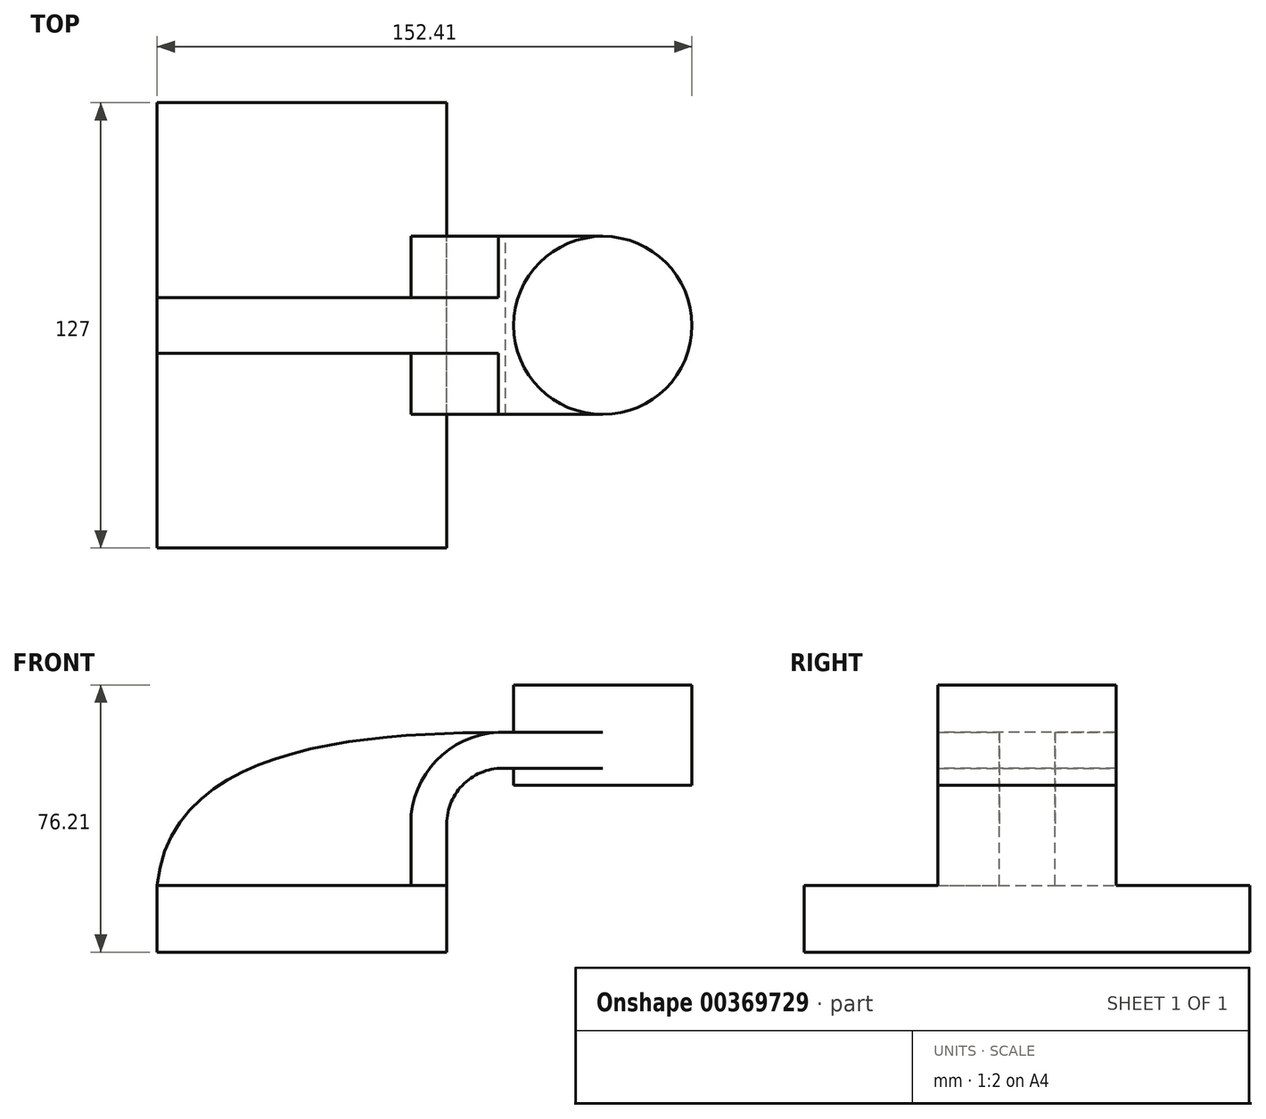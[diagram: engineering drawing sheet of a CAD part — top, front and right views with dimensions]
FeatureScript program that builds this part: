
annotation { "Feature Type Name" : "Feature", "Feature Type Description" : "" }
export const myFeature = defineFeature(function(context is Context, id is Id, definition is map)
    precondition{}
    {
        {
            var Q0;
            Q0=qCreatedBy(makeId("Front.planeOp"),FACE);
            var sketch = newSketch(context, id + "F0", { "sketchPlane" : qUnion([Q0])});
            skLineSegment(sketch, "E0.bottom", {"start": v(-41.27, -9.53) * mm, "end": v(41.28, -9.53) * mm});
            skLineSegment(sketch, "E0.top", {"start": v(-41.28, 9.52) * mm, "end": v(41.28, 9.52) * mm});
            skLineSegment(sketch, "E0.left", {"start": v(-41.28, -9.53) * mm, "end": v(-41.28, 9.52) * mm});
            skLineSegment(sketch, "E0.right", {"start": v(41.28, -9.53) * mm, "end": v(41.28, 9.52) * mm});
            skPoint(sketch, "E0.middle", {"position": v(0, 0) * mm});
            skLineSegment(sketch, "E1.bottom", {"start": v(60.33, 38.1) * mm, "end": v(111.12, 38.1) * mm});
            skLineSegment(sketch, "E1.top", {"start": v(60.33, 66.67) * mm, "end": v(111.12, 66.67) * mm});
            skLineSegment(sketch, "E1.left", {"start": v(60.32, 38.1) * mm, "end": v(60.32, 66.67) * mm});
            skLineSegment(sketch, "E1.right", {"start": v(111.12, 38.1) * mm, "end": v(111.12, 66.67) * mm});
            skPoint(sketch, "E1.middle", {"position": v(85.72, 52.39) * mm});
            skLineSegment(sketch, "E2", {"start": v(41.27, 9.52) * mm, "end": v(41.27, 27.02) * mm});
            skArc(sketch, "E3", {"start": v(41.27, 27.02) * mm, "mid": v(46.22, 38.54) * mm, "end": v(57.98, 42.88) * mm});
            skLineSegment(sketch, "E4", {"start": v(57.98, 42.88) * mm, "end": v(85.72, 42.88) * mm});
            skLineSegment(sketch, "E5.0", {"start": v(58.21, 53.13) * mm, "end": v(85.72, 53.13) * mm});
            skArc(sketch, "E5.1", {"start": v(31.02, 27.02) * mm, "mid": v(39.05, 45.87) * mm, "end": v(58.21, 53.13) * mm});
            skLineSegment(sketch, "E5.2", {"start": v(31.02, 9.52) * mm, "end": v(31.02, 27.02) * mm});
            skLineSegment(sketch, "E6", {"start": v(85.72, 53.13) * mm, "end": v(85.72, 42.88) * mm});
            skFitSpline(sketch, "E7", {"points": [v(-41.28, 9.53) * mm, v(58.21, 53.13) * mm], "startDerivative": vector(12.21, 123.55) * mm, "endDerivative": vector(111.34, 0.22) * mm});
            skLineSegment(sketch, "E8", {"start": v(85.72, 66.67) * mm, "end": v(85.72, 38.1) * mm});
            skSolve(sketch);
        }
        {
            var Q0;
            Q0=makeQuery(id+"F0.imprint","IMPRINT",FACE,{"disambiguationData":[TD([[makeQuery(id+"F0.imprint","IMPRINT",EDGE,{"derivedFrom":sQuery(id+"F0.wireOp",EDGE,"E0.bottom")}),1.0]])]});
            extrude(context, id + "F1", {"entities" : qUnion([Q0]), "endBound" : BoundingType.SYMMETRIC, "depth" : 127 * mm});
        }
        {
            var Q0;
            {var subQ0=sQuery(id+"F0.wireOp",EDGE,"E2");Q0=makeQuery(id+"F0.imprint","IMPRINT",FACE,{"disambiguationData":[TD([[makeQuery(id+"F0.imprint","IMPRINT",EDGE,{"derivedFrom":subQ0}),1.0]])]});}
            var Q1;
            {var subQ0=sQuery(id+"F0.wireOp",EDGE,"E4");var subQ1=sQuery(id+"F0.wireOp",EDGE,"E1.left");var subQ2=makeQuery(id+"F0.imprint","INTERSECT",VERTEX,{"derivedFrom":[subQ1,subQ0]});Q1=makeQuery(id+"F0.imprint","IMPRINT",FACE,{"disambiguationData":[TD([[makeQuery(id+"F0.imprint","IMPRINT",EDGE,{"disambiguationData":[TD([[subQ2,-1.0]])],"derivedFrom":subQ1}),-1.0]])]});}
            extrude(context, id + "F2", {"entities" : qUnion([Q0, Q1]), "operationType" : NewBodyOperationType.ADD, "endBound" : BoundingType.SYMMETRIC, "depth" : 50.8 * mm});
        }
        {
            var Q0;
            {var subQ3=sQuery(id+"F0.wireOp",EDGE,"E5.2");Q0=makeQuery(id+"F0.imprint","IMPRINT",FACE,{"disambiguationData":[TD([[makeQuery(id+"F0.imprint","IMPRINT",EDGE,{"derivedFrom":subQ3}),1.0]])]});}
            extrude(context, id + "F3", {"entities" : qUnion([Q0]), "operationType" : NewBodyOperationType.ADD, "endBound" : BoundingType.SYMMETRIC, "depth" : 15.88 * mm});
        }
        {
            var Q0;
            {var subQ4=sQuery(id+"F0.wireOp",EDGE,"E1.right");Q0=makeQuery(id+"F0.imprint","IMPRINT",FACE,{"disambiguationData":[TD([[makeQuery(id+"F0.imprint","IMPRINT",EDGE,{"derivedFrom":subQ4}),1.0]])]});}
            var Q1;
            Q1=sQuery(id+"F0.wireOp",EDGE,"E8");
            revolve(context, id + "F4", {"operationType" : NewBodyOperationType.ADD, "entities" : qUnion([Q0]), "axis" : qUnion([Q1]), "revolveType" : RevolveType.FULL});
        }
    });
